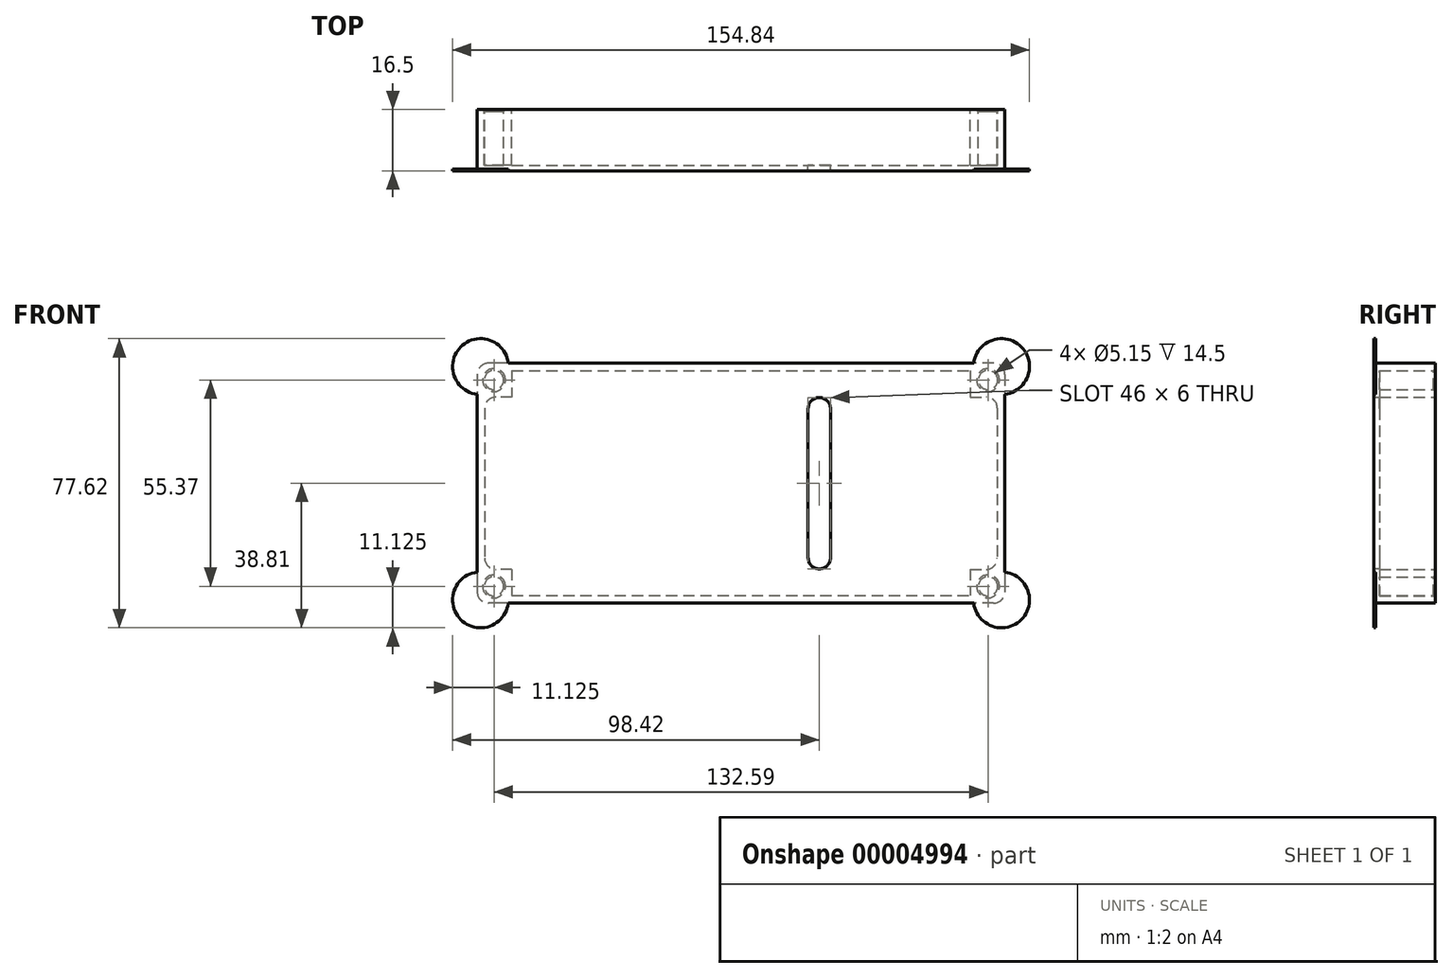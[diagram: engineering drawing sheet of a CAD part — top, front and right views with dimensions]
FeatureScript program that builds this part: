
annotation { "Feature Type Name" : "Feature", "Feature Type Description" : "" }
export const myFeature = defineFeature(function(context is Context, id is Id, definition is map)
    precondition{}
    {
        {
            var Q0;
            Q0=qCreatedBy(makeId("Front.planeOp"),FACE);
            var sketch = newSketch(context, id + "F0", { "sketchPlane" : qUnion([Q0])});
            skLineSegment(sketch, "E0.rect.bottom", {"start": v(61.5, 28) * mm, "end": v(-61.5, 28) * mm});
            skLineSegment(sketch, "E0.rect.top", {"start": v(61.5, -28) * mm, "end": v(-61.5, -28) * mm});
            skLineSegment(sketch, "E0.rect.left", {"start": v(61.5, 28) * mm, "end": v(61.5, -28) * mm});
            skLineSegment(sketch, "E0.rect.right", {"start": v(-61.5, 28) * mm, "end": v(-61.5, -28) * mm});
            skPoint(sketch, "E0.rect.middle", {"position": v(0, 0) * mm});
            skLineSegment(sketch, "E1", {"start": v(0, 28) * mm, "end": v(0, 0) * mm, "construction": true});
            skLineSegment(sketch, "E2", {"start": v(0, 0) * mm, "end": v(-61.5, 0) * mm, "construction": true});
            skCircle(sketch, "E3", {"center": v(-66.3, 27.68) * mm, "radius": 2.58 * mm});
            skCircle(sketch, "E4.MirrorC", {"center": v(66.3, 27.68) * mm, "radius": 2.58 * mm});
            skCircle(sketch, "E5.MirrorC", {"center": v(-66.3, -27.68) * mm, "radius": 2.58 * mm});
            skCircle(sketch, "E6.MirrorC", {"center": v(66.3, -27.68) * mm, "radius": 2.58 * mm});
            skLineSegment(sketch, "E7.rect.bottom", {"start": v(70.8, 32.18) * mm, "end": v(-70.8, 32.18) * mm});
            skLineSegment(sketch, "E7.rect.top", {"start": v(70.8, -32.18) * mm, "end": v(-70.8, -32.18) * mm});
            skLineSegment(sketch, "E7.rect.left", {"start": v(70.8, 32.18) * mm, "end": v(70.8, -32.18) * mm});
            skLineSegment(sketch, "E7.rect.right", {"start": v(-70.8, 32.18) * mm, "end": v(-70.8, -32.18) * mm});
            skSolve(sketch);
        }
        {
            var Q0;
            Q0 = qSketchRegion(id + "F0", true);
            extrude(context, id + "F1", {"entities" : qUnion([Q0]), "depth" : 15 * mm});
        }
        {
            var Q0;
            Q0=makeQuery(id+"F1.opExtrude","CAP_FACE",FACE,{"disambiguationData":[OSD([sQuery(id+"F0.wireOp",EDGE,"E0.rect.bottom"),sQuery(id+"F0.wireOp",EDGE,"E0.rect.top"),sQuery(id+"F0.wireOp",EDGE,"E0.rect.left"),sQuery(id+"F0.wireOp",EDGE,"E0.rect.right"),sQuery(id+"F0.wireOp",EDGE,"E3"),sQuery(id+"F0.wireOp",EDGE,"E4.MirrorC"),sQuery(id+"F0.wireOp",EDGE,"E5.MirrorC"),sQuery(id+"F0.wireOp",EDGE,"E6.MirrorC"),sQuery(id+"F0.wireOp",EDGE,"E7.rect.bottom"),sQuery(id+"F0.wireOp",EDGE,"E7.rect.top"),sQuery(id+"F0.wireOp",EDGE,"E7.rect.left"),sQuery(id+"F0.wireOp",EDGE,"E7.rect.right")])],"isStart":false});
            var sketch = newSketch(context, id + "F2", { "sketchPlane" : qUnion([Q0])});
            skLineSegment(sketch, "E8.0", {"start": v(70.8, 32.18) * mm, "end": v(-70.8, 32.18) * mm});
            skLineSegment(sketch, "E8.1", {"start": v(-70.8, 32.18) * mm, "end": v(-70.8, -32.18) * mm});
            skLineSegment(sketch, "E8.2", {"start": v(70.8, -32.18) * mm, "end": v(-70.8, -32.18) * mm});
            skLineSegment(sketch, "E8.3", {"start": v(70.8, 32.18) * mm, "end": v(70.8, -32.18) * mm});
            skLineSegment(sketch, "E9.bottom", {"start": v(18, 23) * mm, "end": v(24, 23) * mm});
            skLineSegment(sketch, "E9.top", {"start": v(18, -23) * mm, "end": v(24, -23) * mm});
            skLineSegment(sketch, "E9.left", {"start": v(18, 23) * mm, "end": v(18, -23) * mm});
            skLineSegment(sketch, "E9.right", {"start": v(24, 23) * mm, "end": v(24, -23) * mm});
            skLineSegment(sketch, "E10", {"start": v(-70.8, 0) * mm, "end": v(70.8, 0) * mm, "construction": true});
            skLineSegment(sketch, "E11", {"start": v(0, 32.18) * mm, "end": v(0, -32.18) * mm, "construction": true});
            skPoint(sketch, "E12", {"position": v(21, 23) * mm});
            skSolve(sketch);
        }
        {
            var Q0;
            Q0 = qSketchRegion(id + "F2", true);
            extrude(context, id + "F3", {"entities" : qUnion([Q0]), "operationType" : NewBodyOperationType.ADD, "depth" : 1.5 * mm});
        }
        {
            var Q0;
            Q0=makeQuery(id+"F1.opExtrude","CAP_FACE",FACE,{"disambiguationData":[OSD([sQuery(id+"F0.wireOp",EDGE,"E0.rect.bottom"),sQuery(id+"F0.wireOp",EDGE,"E0.rect.top"),sQuery(id+"F0.wireOp",EDGE,"E0.rect.left"),sQuery(id+"F0.wireOp",EDGE,"E0.rect.right"),sQuery(id+"F0.wireOp",EDGE,"E3"),sQuery(id+"F0.wireOp",EDGE,"E4.MirrorC"),sQuery(id+"F0.wireOp",EDGE,"E5.MirrorC"),sQuery(id+"F0.wireOp",EDGE,"E6.MirrorC"),sQuery(id+"F0.wireOp",EDGE,"E7.rect.bottom"),sQuery(id+"F0.wireOp",EDGE,"E7.rect.top"),sQuery(id+"F0.wireOp",EDGE,"E7.rect.left"),sQuery(id+"F0.wireOp",EDGE,"E7.rect.right")])],"isStart":true});
            var sketch = newSketch(context, id + "F4", { "sketchPlane" : qUnion([Q0])});
            skLineSegment(sketch, "E13", {"start": v(0, 28) * mm, "end": v(0, -28) * mm, "construction": true});
            skLineSegment(sketch, "E14", {"start": v(0, 0) * mm, "end": v(-44.75, 0) * mm, "construction": true});
            skLineSegment(sketch, "E15.bottom", {"start": v(-61.5, 23.1) * mm, "end": v(-68.8, 23.1) * mm});
            skLineSegment(sketch, "E15.top", {"start": v(-61.5, -23.11) * mm, "end": v(-68.8, -23.11) * mm});
            skLineSegment(sketch, "E15.left", {"start": v(-61.5, 23.1) * mm, "end": v(-61.5, -23.11) * mm});
            skLineSegment(sketch, "E15.right", {"start": v(-68.8, 23.1) * mm, "end": v(-68.8, -23.11) * mm});
            skCircle(sketch, "E16.0", {"center": v(-66.3, 27.68) * mm, "radius": 2.57 * mm, "construction": true});
            skPoint(sketch, "E17", {"position": v(-66.3, 25.1) * mm});
            skLineSegment(sketch, "E18.MirrorCS", {"start": v(61.5, -23.1) * mm, "end": v(68.8, -23.1) * mm});
            skLineSegment(sketch, "E19.MirrorCS", {"start": v(68.8, 23.11) * mm, "end": v(68.8, -23.11) * mm});
            skLineSegment(sketch, "E20.MirrorCS", {"start": v(61.5, 23.11) * mm, "end": v(61.5, -23.11) * mm});
            skLineSegment(sketch, "E21.MirrorCS", {"start": v(61.5, 23.11) * mm, "end": v(68.8, 23.11) * mm});
            skLineSegment(sketch, "E22.bottom", {"start": v(61.5, -28) * mm, "end": v(-61.5, -28) * mm});
            skLineSegment(sketch, "E22.top", {"start": v(61.5, -30.18) * mm, "end": v(-61.5, -30.19) * mm});
            skLineSegment(sketch, "E22.left", {"start": v(61.5, -28) * mm, "end": v(61.5, -30.18) * mm});
            skLineSegment(sketch, "E22.right", {"start": v(-61.5, -28) * mm, "end": v(-61.5, -30.19) * mm});
            skLineSegment(sketch, "E23.MirrorCS", {"start": v(-61.5, 28) * mm, "end": v(-61.5, 30.19) * mm});
            skLineSegment(sketch, "E24.MirrorCS", {"start": v(61.5, 28) * mm, "end": v(61.5, 30.18) * mm});
            skLineSegment(sketch, "E25.MirrorCS", {"start": v(61.5, 28) * mm, "end": v(-61.5, 28) * mm});
            skLineSegment(sketch, "E26.MirrorCS", {"start": v(61.5, 30.18) * mm, "end": v(-61.5, 30.19) * mm});
            skSolve(sketch);
        }
        {
            var Q0;
            Q0 = qSketchRegion(id + "F4", true);
            var Q1;
            {var subQ0=sQuery(id+"F2.wireOp",EDGE,"E9.bottom");var subQ1=sQuery(id+"F2.wireOp",EDGE,"E9.top");var subQ2=sQuery(id+"F2.wireOp",EDGE,"E9.left");var subQ3=sQuery(id+"F2.wireOp",EDGE,"E9.right");Q1=makeQuery(id+"F3.boolean.opBoolean","SPLIT",FACE,{"disambiguationData":[TD([makeQuery(id+"F1.opExtrude","SWEPT_FACE",FACE,{"disambiguationData":[OSD([sQuery(id+"F0.wireOp",EDGE,"E0.rect.bottom")])]})])],"derivedFrom":makeQuery(id+"F3.opExtrude","CAP_FACE",FACE,{"disambiguationData":[OSD([sQuery(id+"F2.wireOp",EDGE,"E8.0"),sQuery(id+"F2.wireOp",EDGE,"E8.1"),sQuery(id+"F2.wireOp",EDGE,"E8.2"),sQuery(id+"F2.wireOp",EDGE,"E8.3"),subQ0,subQ1,subQ2,subQ3])],"isStart":true})});}
            extrude(context, id + "F5", {"entities" : qUnion([Q0]), "operationType" : NewBodyOperationType.REMOVE, "endBound" : BoundingType.UP_TO_SURFACE, "oppositeDirection" : true, "endBoundEntityFace" : qUnion([Q1]), "depth" : 25 * mm});
        }
        {
            var Q0;
            Q0=makeQuery(id+"F5.boolean.opBoolean","COPY",EDGE,{"derivedFrom":makeQuery(id+"F5.opExtrude","SWEPT_EDGE",EDGE,{"disambiguationData":[OSD([sQuery(id+"F0.wireOp",EDGE,"E0.rect.left"),sQuery(id+"F4.wireOp",EDGE,"E15.bottom"),sQuery(id+"F4.wireOp",EDGE,"E15.left")])]})});
            var Q1;
            Q1=makeQuery(id+"F3.boolean.opBoolean","MERGE",EDGE,{"derivedFrom":[makeQuery(id+"F1.opExtrude","SWEPT_EDGE",EDGE,{"disambiguationData":[OSD([sQuery(id+"F0.wireOp",EDGE,"E7.rect.bottom"),sQuery(id+"F0.wireOp",EDGE,"E7.rect.left")])]}),makeQuery(id+"F3.opExtrude","SWEPT_EDGE",EDGE,{"disambiguationData":[OSD([sQuery(id+"F2.wireOp",EDGE,"E8.0"),sQuery(id+"F2.wireOp",EDGE,"E8.3")])]})]});
            var Q2;
            Q2=makeQuery(id+"F5.boolean.opBoolean","COPY",EDGE,{"derivedFrom":makeQuery(id+"F5.opExtrude","SWEPT_EDGE",EDGE,{"disambiguationData":[OSD([sQuery(id+"F4.wireOp",EDGE,"E15.bottom"),sQuery(id+"F4.wireOp",EDGE,"E15.right")])]})});
            var Q3;
            Q3=makeQuery(id+"F5.boolean.opBoolean","COPY",EDGE,{"derivedFrom":makeQuery(id+"F5.opExtrude","SWEPT_EDGE",EDGE,{"disambiguationData":[OSD([sQuery(id+"F0.wireOp",EDGE,"E0.rect.left"),sQuery(id+"F4.wireOp",EDGE,"E15.top"),sQuery(id+"F4.wireOp",EDGE,"E15.left")])]})});
            var Q4;
            Q4=makeQuery(id+"F5.boolean.opBoolean","COPY",EDGE,{"derivedFrom":makeQuery(id+"F5.opExtrude","SWEPT_EDGE",EDGE,{"disambiguationData":[OSD([sQuery(id+"F4.wireOp",EDGE,"E15.top"),sQuery(id+"F4.wireOp",EDGE,"E15.right")])]})});
            var Q5;
            Q5=makeQuery(id+"F3.boolean.opBoolean","MERGE",EDGE,{"derivedFrom":[makeQuery(id+"F1.opExtrude","SWEPT_EDGE",EDGE,{"disambiguationData":[OSD([sQuery(id+"F0.wireOp",EDGE,"E7.rect.top"),sQuery(id+"F0.wireOp",EDGE,"E7.rect.left")])]}),makeQuery(id+"F3.opExtrude","SWEPT_EDGE",EDGE,{"disambiguationData":[OSD([sQuery(id+"F2.wireOp",EDGE,"E8.2"),sQuery(id+"F2.wireOp",EDGE,"E8.3")])]})]});
            var Q6;
            Q6=makeQuery(id+"F3.boolean.opBoolean","MERGE",EDGE,{"derivedFrom":[makeQuery(id+"F1.opExtrude","SWEPT_EDGE",EDGE,{"disambiguationData":[OSD([sQuery(id+"F0.wireOp",EDGE,"E7.rect.top"),sQuery(id+"F0.wireOp",EDGE,"E7.rect.right")])]}),makeQuery(id+"F3.opExtrude","SWEPT_EDGE",EDGE,{"disambiguationData":[OSD([sQuery(id+"F2.wireOp",EDGE,"E8.1"),sQuery(id+"F2.wireOp",EDGE,"E8.2")])]})]});
            var Q7;
            Q7=makeQuery(id+"F5.boolean.opBoolean","COPY",EDGE,{"derivedFrom":makeQuery(id+"F5.opExtrude","SWEPT_EDGE",EDGE,{"disambiguationData":[OSD([sQuery(id+"F0.wireOp",EDGE,"E0.rect.right"),sQuery(id+"F4.wireOp",EDGE,"E20.MirrorCS"),sQuery(id+"F4.wireOp",EDGE,"E21.MirrorCS")])]})});
            var Q8;
            Q8=makeQuery(id+"F5.boolean.opBoolean","COPY",EDGE,{"derivedFrom":makeQuery(id+"F5.opExtrude","SWEPT_EDGE",EDGE,{"disambiguationData":[OSD([sQuery(id+"F4.wireOp",EDGE,"E19.MirrorCS"),sQuery(id+"F4.wireOp",EDGE,"E21.MirrorCS")])]})});
            var Q9;
            Q9=makeQuery(id+"F3.boolean.opBoolean","MERGE",EDGE,{"derivedFrom":[makeQuery(id+"F1.opExtrude","SWEPT_EDGE",EDGE,{"disambiguationData":[OSD([sQuery(id+"F0.wireOp",EDGE,"E7.rect.bottom"),sQuery(id+"F0.wireOp",EDGE,"E7.rect.right")])]}),makeQuery(id+"F3.opExtrude","SWEPT_EDGE",EDGE,{"disambiguationData":[OSD([sQuery(id+"F2.wireOp",EDGE,"E8.0"),sQuery(id+"F2.wireOp",EDGE,"E8.1")])]})]});
            var Q10;
            Q10=makeQuery(id+"F5.boolean.opBoolean","COPY",EDGE,{"derivedFrom":makeQuery(id+"F5.opExtrude","SWEPT_EDGE",EDGE,{"disambiguationData":[OSD([sQuery(id+"F0.wireOp",EDGE,"E0.rect.right"),sQuery(id+"F4.wireOp",EDGE,"E18.MirrorCS"),sQuery(id+"F4.wireOp",EDGE,"E20.MirrorCS")])]})});
            var Q11;
            Q11=makeQuery(id+"F5.boolean.opBoolean","COPY",EDGE,{"derivedFrom":makeQuery(id+"F5.opExtrude","SWEPT_EDGE",EDGE,{"disambiguationData":[OSD([sQuery(id+"F4.wireOp",EDGE,"E18.MirrorCS"),sQuery(id+"F4.wireOp",EDGE,"E19.MirrorCS")])]})});
            var Q12;
            Q12=makeQuery(id+"F3.opExtrude","SWEPT_EDGE",EDGE,{"disambiguationData":[OSD([sQuery(id+"F2.wireOp",EDGE,"E9.top"),sQuery(id+"F2.wireOp",EDGE,"E9.left")])]});
            var Q13;
            Q13=makeQuery(id+"F3.opExtrude","SWEPT_EDGE",EDGE,{"disambiguationData":[OSD([sQuery(id+"F2.wireOp",EDGE,"E9.top"),sQuery(id+"F2.wireOp",EDGE,"E9.right")])]});
            var Q14;
            Q14=makeQuery(id+"F3.opExtrude","SWEPT_EDGE",EDGE,{"disambiguationData":[OSD([sQuery(id+"F2.wireOp",EDGE,"E9.bottom"),sQuery(id+"F2.wireOp",EDGE,"E9.right")])]});
            var Q15;
            Q15=makeQuery(id+"F3.opExtrude","SWEPT_EDGE",EDGE,{"disambiguationData":[OSD([sQuery(id+"F2.wireOp",EDGE,"E9.bottom"),sQuery(id+"F2.wireOp",EDGE,"E9.left")])]});
            fillet(context, id + "F6", {"entities" : qUnion([Q0, Q1, Q2, Q3, Q4, Q5, Q6, Q7, Q8, Q9, Q10, Q11, Q12, Q13, Q14, Q15]), "radius" : 3 * mm, "tangentPropagation" : true, "allowEdgeOverflow" : false});
        }
        {
            var Q0;
            Q0=makeQuery(id+"F1.opExtrude","CAP_EDGE",EDGE,{"disambiguationData":[OSD([sQuery(id+"F0.wireOp",EDGE,"E5.MirrorC")])],"isStart":true});
            var Q1;
            Q1=makeQuery(id+"F1.opExtrude","CAP_EDGE",EDGE,{"disambiguationData":[OSD([sQuery(id+"F0.wireOp",EDGE,"E3")])],"isStart":true});
            var Q2;
            Q2=makeQuery(id+"F1.opExtrude","CAP_EDGE",EDGE,{"disambiguationData":[OSD([sQuery(id+"F0.wireOp",EDGE,"E6.MirrorC")])],"isStart":true});
            var Q3;
            Q3=makeQuery(id+"F1.opExtrude","CAP_EDGE",EDGE,{"disambiguationData":[OSD([sQuery(id+"F0.wireOp",EDGE,"E4.MirrorC")])],"isStart":true});
            chamfer(context, id + "F7", {"entities" : qUnion([Q0, Q1, Q2, Q3]), "width" : 0.5 * mm, "tangentPropagation" : true});
        }
        {
            var Q0;
            Q0=makeQuery(id+"F3.opExtrude","CAP_FACE",FACE,{"disambiguationData":[OSD([sQuery(id+"F2.wireOp",EDGE,"E8.0"),sQuery(id+"F2.wireOp",EDGE,"E8.1"),sQuery(id+"F2.wireOp",EDGE,"E8.2"),sQuery(id+"F2.wireOp",EDGE,"E8.3"),sQuery(id+"F2.wireOp",EDGE,"E9.bottom"),sQuery(id+"F2.wireOp",EDGE,"E9.top"),sQuery(id+"F2.wireOp",EDGE,"E9.left"),sQuery(id+"F2.wireOp",EDGE,"E9.right")])],"isStart":false});
            var sketch = newSketch(context, id + "F8", { "sketchPlane" : qUnion([Q0])});
            skCircle(sketch, "E27", {"center": v(69.92, -31.3) * mm, "radius": 7.5 * mm});
            skLineSegment(sketch, "E28", {"start": v(0, -32.18) * mm, "end": v(0, 32.18) * mm, "construction": true});
            skLineSegment(sketch, "E29", {"start": v(0, 0) * mm, "end": v(70.8, 0) * mm, "construction": true});
            skCircle(sketch, "E30.MirrorC", {"center": v(-69.92, -31.3) * mm, "radius": 7.5 * mm});
            skCircle(sketch, "E31.MirrorC", {"center": v(69.92, 31.3) * mm, "radius": 7.5 * mm});
            skCircle(sketch, "E32.MirrorC", {"center": v(-69.92, 31.3) * mm, "radius": 7.5 * mm});
            skSolve(sketch);
        }
        {
            var Q0;
            Q0 = qSketchRegion(id + "F8", true);
            extrude(context, id + "F9", {"entities" : qUnion([Q0]), "operationType" : NewBodyOperationType.ADD, "oppositeDirection" : true, "depth" : 0.5 * mm});
        }
    });
